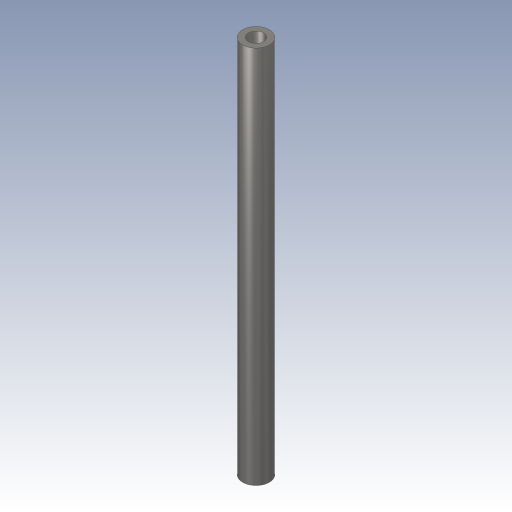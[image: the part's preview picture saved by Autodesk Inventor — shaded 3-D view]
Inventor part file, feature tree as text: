
AUTODESK INVENTOR PART (.ipt)
format: ipt  version: 2023.3 (Build 273359000, 359)  size: 161,280 bytes
history: native  units: in
note: dims shown in document units (in); Inventor stores cm internally (conversion verified against a paired STEP export)
features: extrude x1, sketch x1
ambient origin geometry x8: Origin, YZ Plane, XZ Plane, XY Plane, X Axis, Y Axis, Z Axis, Center Point
bodies: Body1 (feature_tree)
feature tree (2):
  extrude  "Extrusion4"  Depth=0.3937in
  sketch  "Skizze6"  dims[d30=0.0276in d31=0.0157in d32=0.3937in d33=0.0in]
